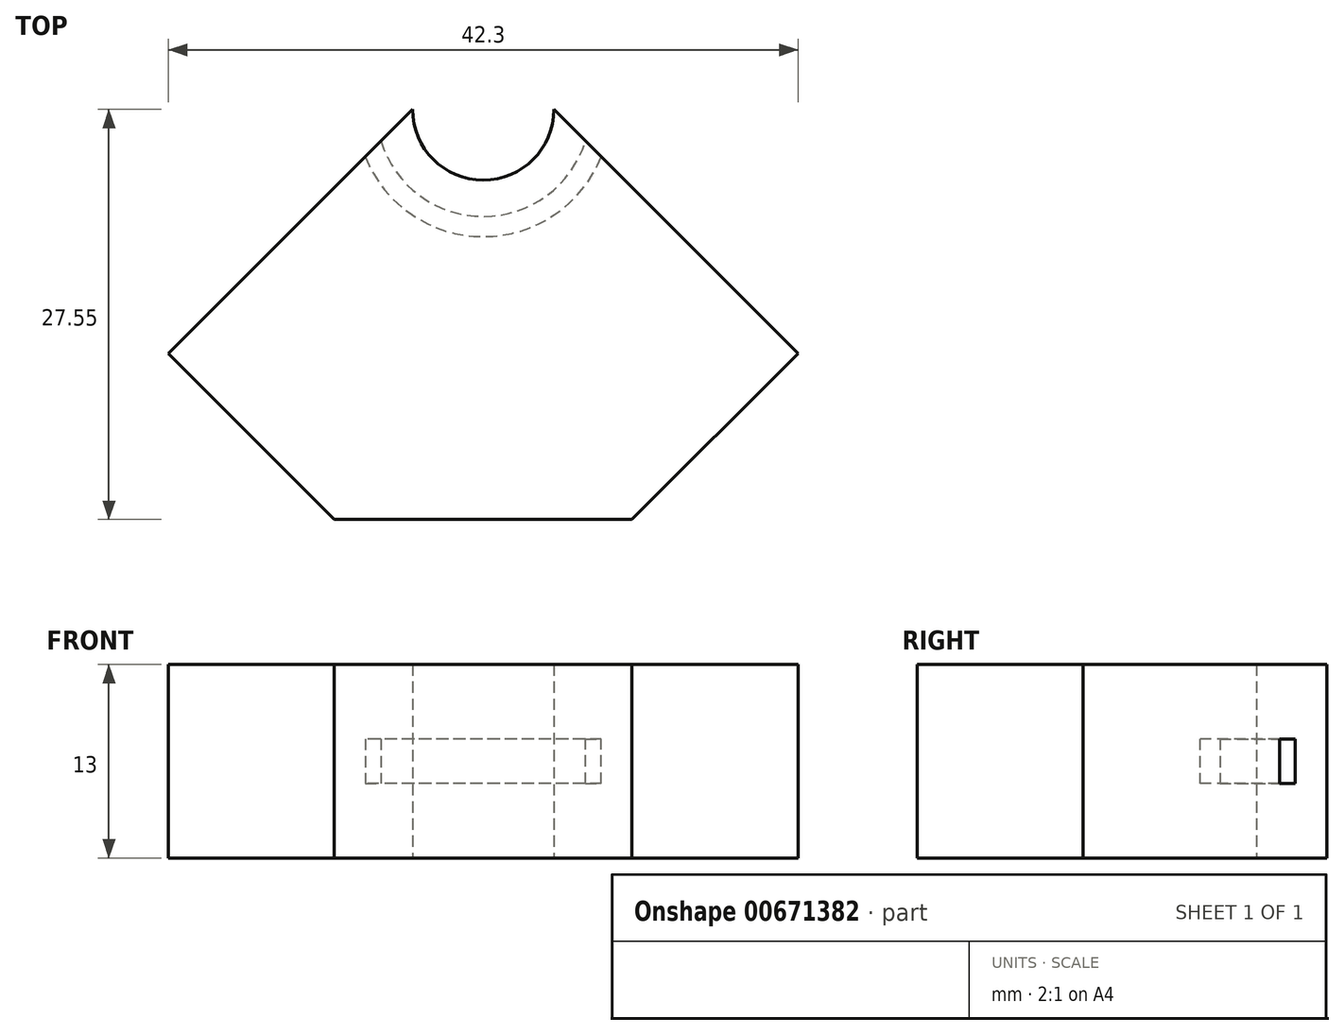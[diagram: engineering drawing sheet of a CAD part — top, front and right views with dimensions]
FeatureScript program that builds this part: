
annotation { "Feature Type Name" : "Feature", "Feature Type Description" : "" }
export const myFeature = defineFeature(function(context is Context, id is Id, definition is map)
    precondition{}
    {
        {
            var Q0;
            Q0=qCreatedBy(makeId("Top.planeOp"),FACE);
            var sketch = newSketch(context, id + "F0", { "sketchPlane" : qUnion([Q0])});
            skLineSegment(sketch, "E0", {"start": v(0, 0) * mm, "end": v(0, 43.84) * mm, "construction": true});
            skLineSegment(sketch, "E1", {"start": v(4.75, 27.55) * mm, "end": v(21.15, 11.15) * mm});
            skLineSegment(sketch, "E2", {"start": v(21.15, 11.15) * mm, "end": v(10, 0) * mm});
            skLineSegment(sketch, "E3", {"start": v(10, 0) * mm, "end": v(0, 0) * mm});
            skLineSegment(sketch, "E4.MirrorCS", {"start": v(-10, 0) * mm, "end": v(0, 0) * mm});
            skLineSegment(sketch, "E5.MirrorCS", {"start": v(-4.75, 27.55) * mm, "end": v(-21.15, 11.15) * mm});
            skLineSegment(sketch, "E6.MirrorCS", {"start": v(-21.15, 11.15) * mm, "end": v(-10, 0) * mm});
            skArc(sketch, "E7", {"start": v(-4.75, 27.55) * mm, "mid": v(0, 22.8) * mm, "end": v(4.75, 27.55) * mm});
            skLineSegment(sketch, "E8", {"start": v(0, 27.55) * mm, "end": v(4.75, 27.55) * mm, "construction": true});
            skPoint(sketch, "E9.orphan", {"position": v(0, 32.3) * mm});
            skSolve(sketch);
        }
        {
            var Q0;
            Q0 = qSketchRegion(id + "F0", true);
            var Q1;
            Q1 = qConstructionFilter(qBodyType(qCreatedBy(id + "F0" ,EDGE), BodyType.WIRE), ConstructionObject.NO);
            extrude(context, id + "F1", {"entities" : qUnion([Q0]), "surfaceEntities" : qUnion([Q1]), "depth" : 13 * mm, "offsetDistance" : 25 * mm});
        }
        {
            var Q0;
            Q0=makeQuery(id+"F1.opExtrude","SWEPT_FACE",FACE,{"disambiguationData":[OSD([sQuery(id+"F0.wireOp",EDGE,"E1")])]});
            var sketch = newSketch(context, id + "F2", { "sketchPlane" : qUnion([Q0])});
            skLineSegment(sketch, "E10.bottom", {"start": v(13.12, 5) * mm, "end": v(11.62, 5) * mm});
            skLineSegment(sketch, "E10.top", {"start": v(13.12, 8) * mm, "end": v(11.62, 8) * mm});
            skLineSegment(sketch, "E10.left", {"start": v(13.12, 5) * mm, "end": v(13.12, 8) * mm});
            skLineSegment(sketch, "E10.right", {"start": v(11.62, 5) * mm, "end": v(11.62, 8) * mm});
            skPoint(sketch, "E10.middle", {"position": v(12.37, 6.5) * mm});
            skPoint(sketch, "E10.middle.positionSnap0", {"position": v(-7.07, 6.5) * mm});
            skPoint(sketch, "E10.centerSnap0", {"position": v(-7.07, 6.5) * mm});
            skSolve(sketch);
        }
        {
            var Q0;
            Q0 = qSketchRegion(id + "F2", true);
            var Q1;
            Q1=makeQuery(id+"F1.opExtrude","CAP_EDGE",EDGE,{"disambiguationData":[OSD([sQuery(id+"F0.wireOp",EDGE,"E7")])],"isStart":false});
            sweep(context, id + "F3", {"operationType" : NewBodyOperationType.REMOVE, "profiles" : qUnion([Q0]), "path" : qUnion([Q1])});
        }
    });
